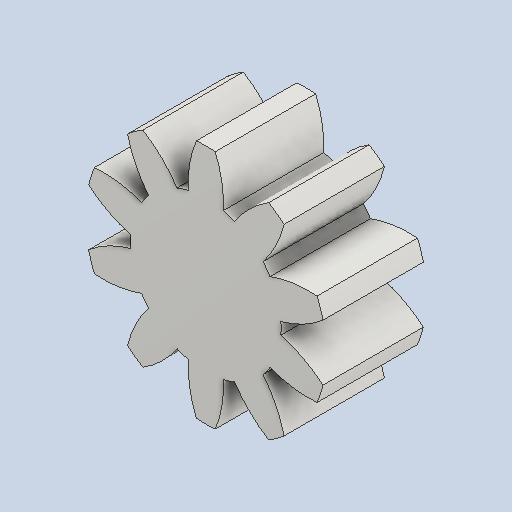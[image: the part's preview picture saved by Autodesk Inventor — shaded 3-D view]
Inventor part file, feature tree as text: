
AUTODESK INVENTOR PART (.ipt)
format: ipt  version: 2023 (Build 270158000, 158)  size: 202,752 bytes
history: native  units: mm (DEFAULTED — no unit token found)
features: plane x3, other x3, sketch x2, extrude x1
ambient origin geometry x8: Origin, YZ Plane, XZ Plane, XY Plane, X Axis, Y Axis, Z Axis, Center Point
bodies: Solid1 (feature_tree)
feature tree (9):
  extrude  "Extrusion1"  Depth=10.0mm TaperAngle=0.0deg
  plane  "Work Plane2"
  plane  "Work Plane8"
  plane  "Work Plane9"
  other  "Spur Gear"
  sketch  "Sketch1"  dims[d0=24.0mm d1=10.0mm d2=0.0mm]
  sketch  "Sketch2"  dims[d3=20.0mm d4=10.0mm d5=0.0mm d16=40.0mm d17=0.0mm d34=3.141593mm d39=0.0mm d41=0.0mm d43=40.0mm d46=40.0mm d47=0.0mm d48=0.0mm]
  other  "Srf1"
  other  "Pitch Diameter"
